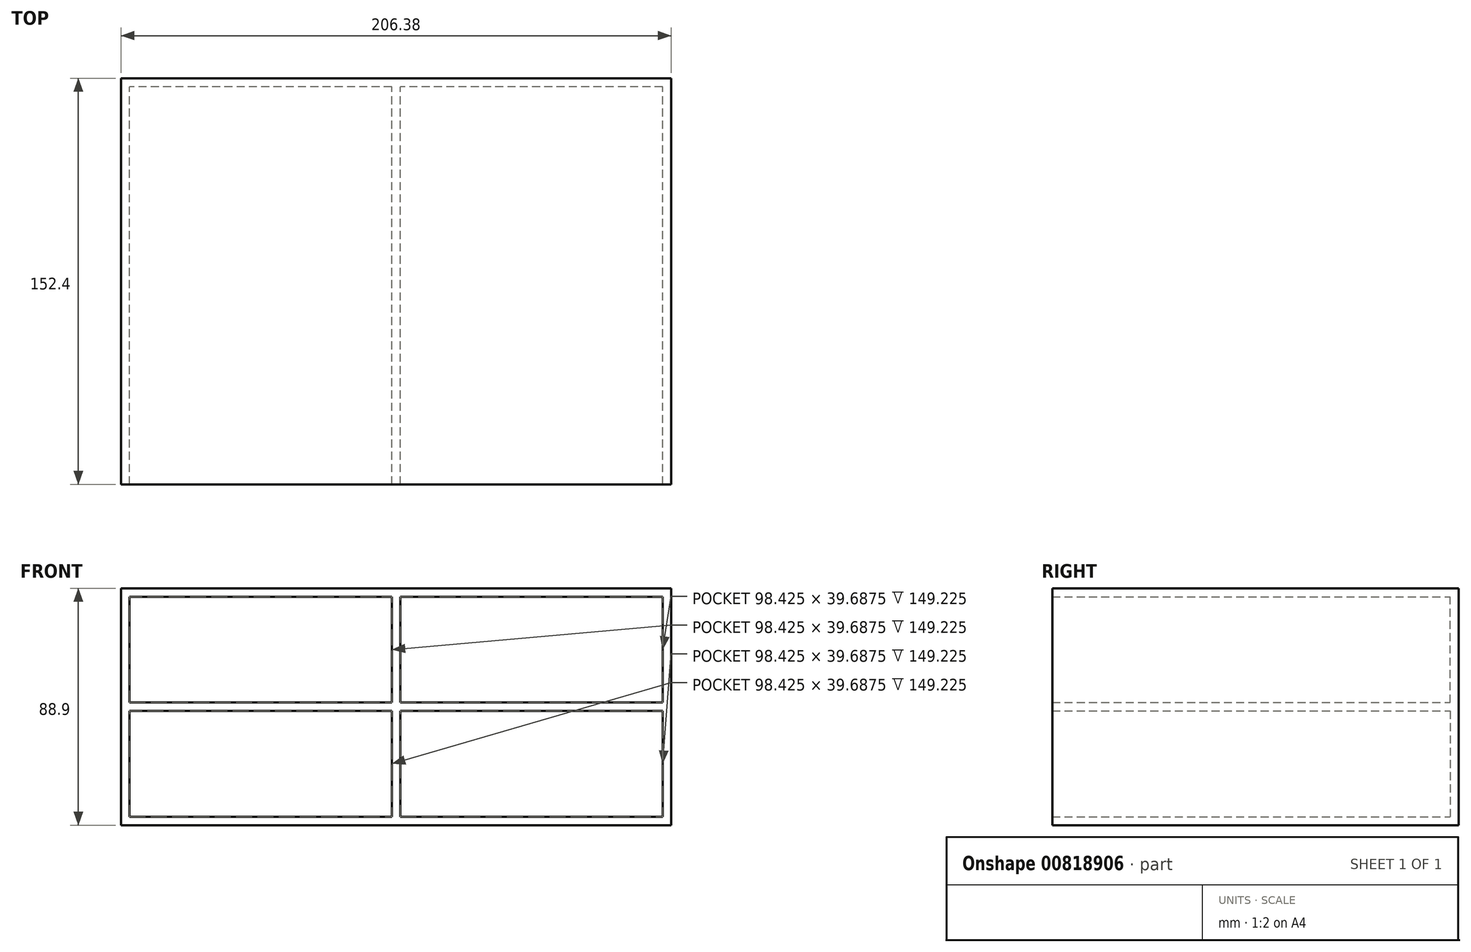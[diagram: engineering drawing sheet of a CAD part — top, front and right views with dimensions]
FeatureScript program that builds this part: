
annotation { "Feature Type Name" : "Feature", "Feature Type Description" : "" }
export const myFeature = defineFeature(function(context is Context, id is Id, definition is map)
    precondition{}
    {
        {
            var Q0;
            Q0=qCreatedBy(makeId("Front.planeOp"),FACE);
            var sketch = newSketch(context, id + "F0", { "sketchPlane" : qUnion([Q0])});
            skLineSegment(sketch, "E0.bottom", {"start": v(-103.19, -44.45) * mm, "end": v(103.19, -44.45) * mm});
            skLineSegment(sketch, "E0.top", {"start": v(-103.19, 44.45) * mm, "end": v(103.19, 44.45) * mm});
            skLineSegment(sketch, "E0.left", {"start": v(-103.19, -44.45) * mm, "end": v(-103.19, 44.45) * mm});
            skLineSegment(sketch, "E0.right", {"start": v(103.19, -44.45) * mm, "end": v(103.19, 44.45) * mm});
            skPoint(sketch, "E0.middle", {"position": v(0, 0) * mm});
            skLineSegment(sketch, "E1.0", {"start": v(-100.01, -1.59) * mm, "end": v(-1.59, -1.59) * mm});
            skLineSegment(sketch, "E2.0", {"start": v(-100.01, 1.59) * mm, "end": v(-1.59, 1.59) * mm});
            skLineSegment(sketch, "E3.0", {"start": v(-1.59, 41.27) * mm, "end": v(-1.59, 1.59) * mm});
            skLineSegment(sketch, "E4.0", {"start": v(1.59, 41.27) * mm, "end": v(1.59, 1.59) * mm});
            skLineSegment(sketch, "E5.0", {"start": v(-100.01, -41.27) * mm, "end": v(-1.59, -41.28) * mm});
            skLineSegment(sketch, "E6.0", {"start": v(100.01, -41.28) * mm, "end": v(100.01, -1.59) * mm});
            skLineSegment(sketch, "E7.0", {"start": v(-100.01, 41.27) * mm, "end": v(-1.59, 41.27) * mm});
            skLineSegment(sketch, "E8.0", {"start": v(-100.01, -41.27) * mm, "end": v(-100.01, -1.59) * mm});
            skLineSegment(sketch, "E9.trimOffspring", {"start": v(-100.01, 1.59) * mm, "end": v(-100.01, 41.27) * mm});
            skLineSegment(sketch, "E10.trimOffspring", {"start": v(1.59, -41.28) * mm, "end": v(100.01, -41.28) * mm});
            skLineSegment(sketch, "E11.trimOffspring", {"start": v(100.01, 1.59) * mm, "end": v(100.01, 41.27) * mm});
            skLineSegment(sketch, "E12.trimOffspring", {"start": v(1.59, 41.27) * mm, "end": v(100.01, 41.27) * mm});
            skLineSegment(sketch, "E13.trimOffspring", {"start": v(1.59, -1.59) * mm, "end": v(1.59, -41.28) * mm});
            skLineSegment(sketch, "E14.trimOffspring", {"start": v(1.59, 1.59) * mm, "end": v(100.01, 1.59) * mm});
            skLineSegment(sketch, "E15.trimOffspring", {"start": v(-1.59, -1.59) * mm, "end": v(-1.59, -41.28) * mm});
            skLineSegment(sketch, "E16.trimOffspring", {"start": v(1.59, -1.59) * mm, "end": v(100.01, -1.59) * mm});
            skSolve(sketch);
        }
        {
            var Q0;
            Q0=makeQuery(id+"F0.imprint","IMPRINT",FACE,{"disambiguationData":[TD([[makeQuery(id+"F0.imprint","IMPRINT",EDGE,{"derivedFrom":sQuery(id+"F0.wireOp",EDGE,"E0.bottom")}),1.0]])]});
            var Q1;
            Q1=makeQuery(id+"F0.imprint","IMPRINT",FACE,{"disambiguationData":[TD([[makeQuery(id+"F0.imprint","IMPRINT",EDGE,{"derivedFrom":sQuery(id+"F0.wireOp",EDGE,"E1.0")}),-1.0]])]});
            var Q2;
            Q2=makeQuery(id+"F0.imprint","IMPRINT",FACE,{"disambiguationData":[TD([[makeQuery(id+"F0.imprint","IMPRINT",EDGE,{"derivedFrom":sQuery(id+"F0.wireOp",EDGE,"E2.0")}),1.0]])]});
            var Q3;
            Q3=makeQuery(id+"F0.imprint","IMPRINT",FACE,{"disambiguationData":[TD([[makeQuery(id+"F0.imprint","IMPRINT",EDGE,{"derivedFrom":sQuery(id+"F0.wireOp",EDGE,"E4.0")}),1.0]])]});
            var Q4;
            Q4=makeQuery(id+"F0.imprint","IMPRINT",FACE,{"disambiguationData":[TD([[makeQuery(id+"F0.imprint","IMPRINT",EDGE,{"derivedFrom":sQuery(id+"F0.wireOp",EDGE,"E6.0")}),1.0]])]});
            extrude(context, id + "F1", {"entities" : qUnion([Q0, Q1, Q2, Q3, Q4]), "depth" : 3.17 * mm, "offsetDistance" : 25.4 * mm});
        }
        {
            var Q0;
            Q0 = qSketchRegion(id + "F0", true);
            extrude(context, id + "F2", {"entities" : qUnion([Q0]), "operationType" : NewBodyOperationType.ADD, "depth" : 152.4 * mm, "offsetDistance" : 25.4 * mm});
        }
    });
